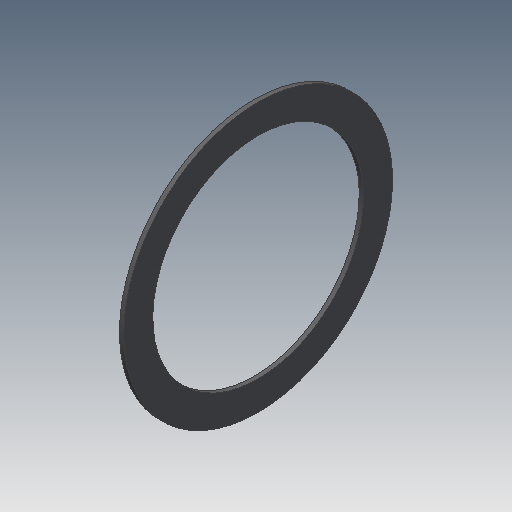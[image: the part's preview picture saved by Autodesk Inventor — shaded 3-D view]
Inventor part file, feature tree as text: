
AUTODESK INVENTOR PART (.ipt)
format: ipt  version: 2019.4 (Build 234330000, 330)  size: 103,424 bytes
history: native  units: mm
features: other x7, revolve x1, sketch x1
ambient origin geometry x8: Origin, YZ Plane, XZ Plane, XY Plane, X Axis, Y Axis, Z Axis, Center Point
bodies: Solid1 (feature_tree)
feature tree (9):
  revolve  "Revolution1"  [1 undecoded]
  other  "ip_st_1_XY"
  other  "ip_st_1_YZ"
  other  "ip_st_1_ZX"
  other  "ip_st_1_X"
  other  "ip_st_1_Y"
  other  "ip_st_1_Z"
  other  "ip_st_1_Center"
  sketch  "Sketch_1"  dims[d0=360.0deg d1=0.0mm]
note: 1 required parameter value undecoded (feature->parameter linkage not recoverable at this tier; creation-order binding heuristic only, values carry confidence <= 0.55)
